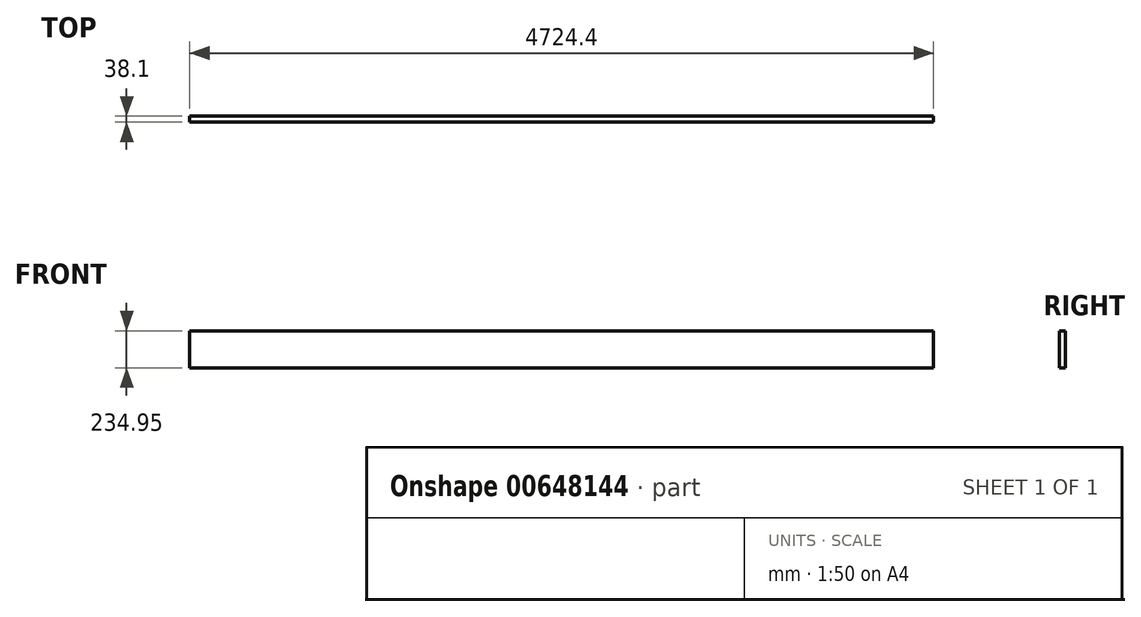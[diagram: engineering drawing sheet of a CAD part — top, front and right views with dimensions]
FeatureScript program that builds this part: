
annotation { "Feature Type Name" : "Feature", "Feature Type Description" : "" }
export const myFeature = defineFeature(function(context is Context, id is Id, definition is map)
    precondition{}
    {
        {
            var Q0;
            Q0=qCreatedBy(makeId("Right.planeOp"),FACE);
            var sketch = newSketch(context, id + "F0", { "sketchPlane" : qUnion([Q0])});
            skLineSegment(sketch, "E0.bottom", {"start": v(0, 0) * mm, "end": v(-38.1, 0) * mm});
            skLineSegment(sketch, "E0.top", {"start": v(0, 234.95) * mm, "end": v(-38.1, 234.95) * mm});
            skLineSegment(sketch, "E0.left", {"start": v(0, 0) * mm, "end": v(0, 234.95) * mm});
            skLineSegment(sketch, "E0.right", {"start": v(-38.1, 0) * mm, "end": v(-38.1, 234.95) * mm});
            skSolve(sketch);
        }
        {
            var Q0;
            Q0 = qSketchRegion(id + "F0", true);
            extrude(context, id + "F1", {"entities" : qUnion([Q0]), "depth" : 4724.4 * mm, "offsetDistance" : 25.4 * mm});
        }
    });
